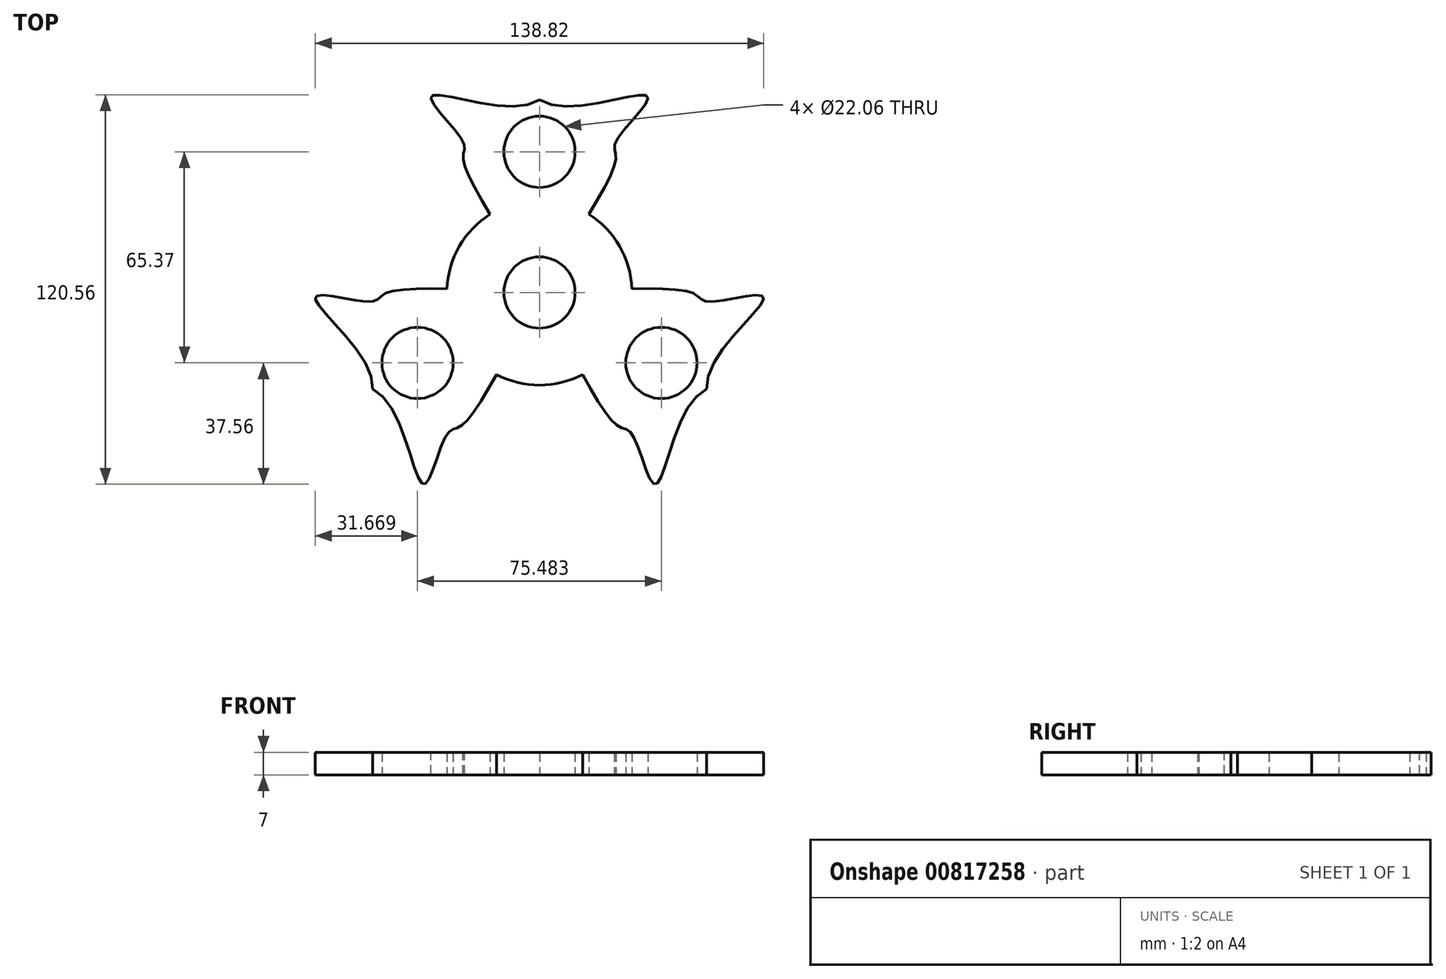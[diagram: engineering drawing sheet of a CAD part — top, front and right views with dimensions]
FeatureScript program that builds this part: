
annotation { "Feature Type Name" : "Feature", "Feature Type Description" : "" }
export const myFeature = defineFeature(function(context is Context, id is Id, definition is map)
    precondition{}
    {
        {
            var Q0;
            Q0=qCreatedBy(makeId("Top.planeOp"),FACE);
            var sketch = newSketch(context, id + "F0", { "sketchPlane" : qUnion([Q0])});
            skCircle(sketch, "E0", {"center": v(0, 43.58) * mm, "radius": 11.03 * mm});
            skCircle(sketch, "E1", {"center": v(0, 0) * mm, "radius": 11.03 * mm});
            skSolve(sketch);
        }
        {
            var Q0;
            Q0=qCreatedBy(makeId("Top.planeOp"),FACE);
            var sketch = newSketch(context, id + "F1", { "sketchPlane" : qUnion([Q0])});
            skFitSpline(sketch, "E2", {"points": [v(0, 0) * mm, v(-23.63, 41.43) * mm, v(-23.63, 46.65) * mm, v(-33.45, 60.76) * mm, v(0, 59.69) * mm, v(12.28, 68.13) * mm], "startDerivative": vector(-98.6, 161.27) * mm, "endDerivative": vector(113.89, -125) * mm});
            skLineSegment(sketch, "E3", {"start": v(0, 0) * mm, "end": v(0, 59.69) * mm});
            skFitSpline(sketch, "E4.MirrorCS", {"points": [v(0, 0) * mm, v(23.63, 41.43) * mm, v(23.63, 46.65) * mm, v(33.45, 60.76) * mm, v(0, 59.69) * mm, v(-12.28, 68.13) * mm], "startDerivative": vector(98.6, 161.27) * mm, "endDerivative": vector(-113.89, -125) * mm});
            skSolve(sketch);
        }
        {
            var Q0;
            {var subQ1=sQuery(id+"F1.wireOp",EDGE,"E3");Q0=makeQuery(id+"F1.imprint","IMPRINT",FACE,{"disambiguationData":[TD([[makeQuery(id+"F1.imprint","IMPRINT",EDGE,{"derivedFrom":subQ1}),1.0]])]});}
            var Q1;
            {var subQ0=sQuery(id+"F1.wireOp",EDGE,"E3");Q1=makeQuery(id+"F1.imprint","IMPRINT",FACE,{"disambiguationData":[TD([[makeQuery(id+"F1.imprint","IMPRINT",EDGE,{"derivedFrom":subQ0}),-1.0]])]});}
            extrude(context, id + "F2", {"entities" : qUnion([Q0, Q1]), "depth" : 7 * mm, "offsetDistance" : 25 * mm});
        }
        {
            var Q0;
            Q0=makeQuery(id+"F0.imprint","IMPRINT",FACE,{"disambiguationData":[TD([[makeQuery(id+"F0.imprint","IMPRINT",EDGE,{"derivedFrom":sQuery(id+"F0.wireOp",EDGE,"E0")}),1.0]])]});
            extrude(context, id + "F3", {"entities" : qUnion([Q0]), "operationType" : NewBodyOperationType.REMOVE, "depth" : 45.6 * mm, "offsetDistance" : 25 * mm});
        }
        {
            var Q0;
            Q0=makeQuery(id+"F2.opExtrude","SWEPT_BODY",BODY,{"disambiguationData":[OSD([sQuery(id+"F1.wireOp",EDGE,"E2"),sQuery(id+"F1.wireOp",EDGE,"E4.MirrorCS")])]});
            var Q1;
            {var subQ0=sQuery(id+"F1.wireOp",EDGE,"E4.MirrorCS");var subQ1=sQuery(id+"F1.wireOp",EDGE,"E3");var subQ2=sQuery(id+"F1.wireOp",EDGE,"E2");Q1=makeQuery(id+"F2.opExtrude","SWEPT_EDGE",EDGE,{"disambiguationData":[OSD([subQ2,subQ1,subQ0]),TDD([makeQuery(id+"F1.imprint","INTERSECT",VERTEX,{"disambiguationData":[OD(0.0)],"derivedFrom":[subQ2,subQ1,subQ0]})])]});}
            circularPattern(context, id + "F4", {"entities" : qUnion([Q0]), "axis" : qUnion([Q1]), "angle" : 360 * degree, "instanceCount" : 3, "equalSpace" : true});
        }
        {
            var Q0;
            Q0=qCreatedBy(makeId("Top.planeOp"),FACE);
            var sketch = newSketch(context, id + "F5", { "sketchPlane" : qUnion([Q0])});
            skCircle(sketch, "E5", {"center": v(0, 0) * mm, "radius": 28.65 * mm});
            skSolve(sketch);
        }
        {
            var Q0;
            Q0=makeQuery(id+"F5.imprint","IMPRINT",FACE,{"disambiguationData":[TD([[makeQuery(id+"F5.imprint","IMPRINT",EDGE,{"derivedFrom":sQuery(id+"F5.wireOp",EDGE,"E5")}),1.0]])]});
            extrude(context, id + "F6", {"entities" : qUnion([Q0]), "operationType" : NewBodyOperationType.ADD, "depth" : 7 * mm, "offsetDistance" : 25 * mm});
        }
        {
            var Q0;
            Q0=makeQuery(id+"F0.imprint","IMPRINT",FACE,{"disambiguationData":[TD([[makeQuery(id+"F0.imprint","IMPRINT",EDGE,{"derivedFrom":sQuery(id+"F0.wireOp",EDGE,"E1")}),1.0]])]});
            extrude(context, id + "F7", {"entities" : qUnion([Q0]), "operationType" : NewBodyOperationType.REMOVE, "depth" : 25 * mm, "offsetDistance" : 25 * mm});
        }
    });
